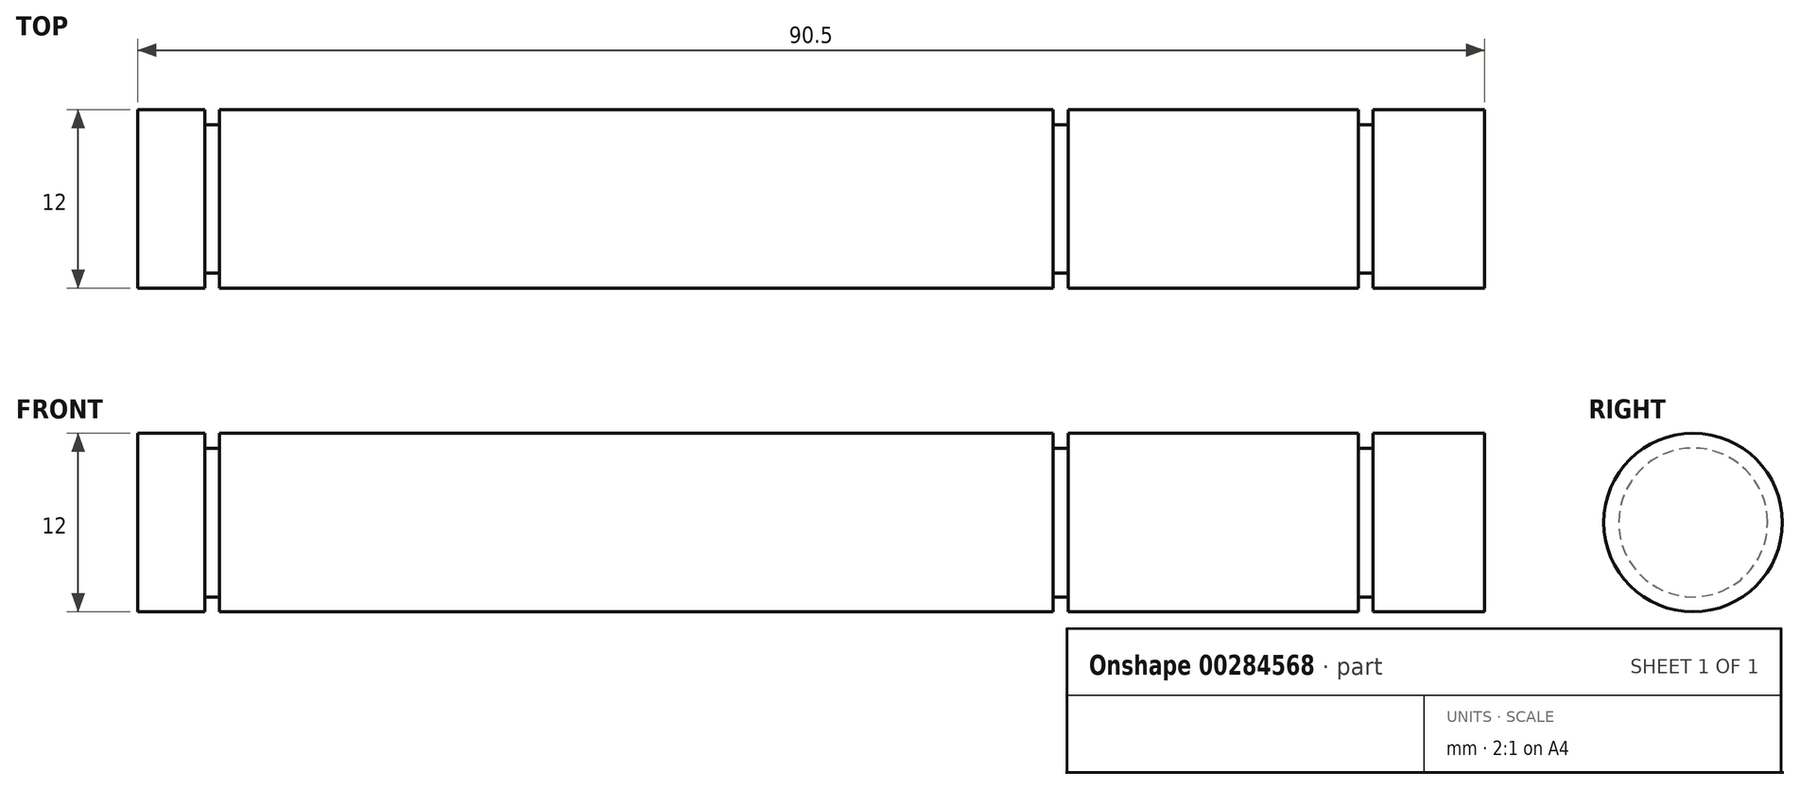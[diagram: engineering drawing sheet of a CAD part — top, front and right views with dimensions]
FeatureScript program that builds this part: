
annotation { "Feature Type Name" : "Feature", "Feature Type Description" : "" }
export const myFeature = defineFeature(function(context is Context, id is Id, definition is map)
    precondition{}
    {
        {
            var Q0;
            Q0=qCreatedBy(makeId("Front.planeOp"),FACE);
            var sketch = newSketch(context, id + "F0", { "sketchPlane" : qUnion([Q0])});
            skLineSegment(sketch, "E0", {"start": v(90.5, 0) * mm, "end": v(90.5, -6) * mm});
            skLineSegment(sketch, "E1", {"start": v(90.5, -6) * mm, "end": v(0, -6) * mm});
            skLineSegment(sketch, "E2", {"start": v(0, -6) * mm, "end": v(0, 0) * mm});
            skLineSegment(sketch, "E3", {"start": v(0, 0) * mm, "end": v(4.5, 0) * mm});
            skLineSegment(sketch, "E4", {"start": v(4.5, 0) * mm, "end": v(4.5, -1) * mm});
            skLineSegment(sketch, "E5", {"start": v(4.5, -1) * mm, "end": v(5.5, -1) * mm});
            skLineSegment(sketch, "E6", {"start": v(5.5, -1) * mm, "end": v(5.5, 0) * mm});
            skLineSegment(sketch, "E7", {"start": v(5.5, 0) * mm, "end": v(61.5, 0) * mm});
            skLineSegment(sketch, "E8", {"start": v(61.5, 0) * mm, "end": v(61.5, -1) * mm});
            skLineSegment(sketch, "E9", {"start": v(61.5, -1) * mm, "end": v(62.5, -1) * mm});
            skLineSegment(sketch, "E10", {"start": v(62.5, -1) * mm, "end": v(62.5, 0) * mm});
            skLineSegment(sketch, "E11", {"start": v(62.5, 0) * mm, "end": v(64.5, 0) * mm});
            skLineSegment(sketch, "E12", {"start": v(0, -6) * mm, "end": v(94.95, -6) * mm, "construction": true});
            skLineSegment(sketch, "E13", {"start": v(65.5, 0) * mm, "end": v(65.5, -1) * mm, "construction": true});
            skLineSegment(sketch, "E14", {"start": v(65.5, -1) * mm, "end": v(64.5, -1) * mm, "construction": true});
            skLineSegment(sketch, "E15", {"start": v(64.5, -1) * mm, "end": v(64.5, 0) * mm, "construction": true});
            skLineSegment(sketch, "E16.trimOffspring", {"start": v(64.5, 0) * mm, "end": v(82, 0) * mm});
            skLineSegment(sketch, "E17", {"start": v(82, 0) * mm, "end": v(82, -1) * mm});
            skLineSegment(sketch, "E18", {"start": v(82, -1) * mm, "end": v(83, -1) * mm});
            skLineSegment(sketch, "E19", {"start": v(83, -1) * mm, "end": v(83, 0) * mm});
            skLineSegment(sketch, "E20.trimOffspring", {"start": v(83, 0) * mm, "end": v(90.5, 0) * mm});
            skSolve(sketch);
        }
        {
            var Q0;
            Q0=qSketchRegion(id+"F0",true);
            var Q1;
            Q1=sQuery(id+"F0.wireOp",EDGE,"E12");
            revolve(context, id + "F1", {"entities" : qUnion([Q0]), "axis" : qUnion([Q1]), "revolveType" : RevolveType.FULL});
        }
    });
